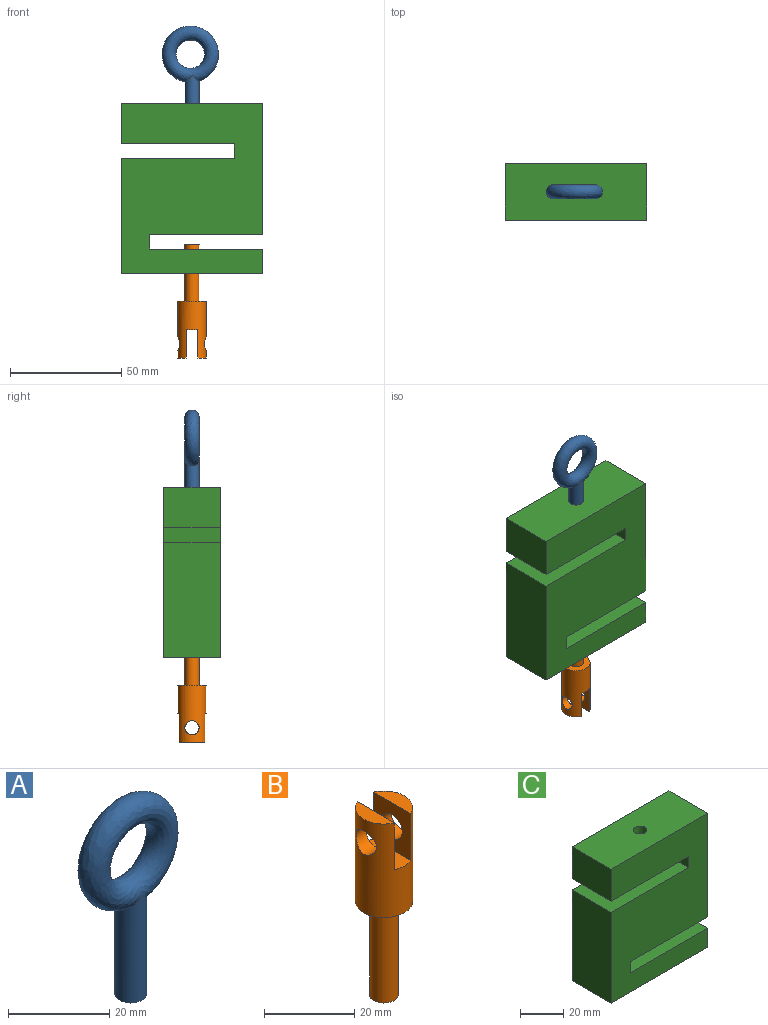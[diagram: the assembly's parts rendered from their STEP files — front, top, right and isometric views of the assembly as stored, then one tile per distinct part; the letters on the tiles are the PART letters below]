
ASSEMBLY  parts=3 mates=2
PART A: 3 faces, bbox 25.1x6.4x47.5 mm
  f0: cylinder r=3.17mm len=25.4mm, axis (0,0,1), area 474.5mm2, adj f1,f2
  f1: plane 6.35x6.35mm, normal (0,0,-1), area 31.7mm2, adj f0
  f2: bspline ~25.26x25.05mm, area 1164.4mm2, adj f0
PART B: 11 faces, bbox 12.7x12.7x50.8 mm
  f0: plane 11.64x3.81mm, normal (0,0,1), area 32mm2, adj f1,f4
  f1: cylinder r=6.35mm len=25.4mm, axis (0,0,-1), area 815.1mm2, adj f0,f2,f3,f4,f5,f6,f7,f8
  f2: plane 11.64x3.81mm, normal (0,0,1), area 32mm2, adj f1,f5
  f3: plane 12.7x12.7mm, normal (0,0,-1), area 95mm2, adj f1,f9
  f4: plane 12.7x11.64mm, normal (-1,0,0), area 116.2mm2, adj f0,f1,f6,f8
  f5: plane 12.7x11.64mm, normal (1,0,0), area 116.2mm2, adj f1,f2,f6,f7
  f6: plane 12.7x5.08mm, normal (0,0,1), area 62.8mm2, adj f1,f4,f5
  f7: cylinder r=3.17mm len=6.35mm, axis (1,0,0), area 67.7mm2, adj f1,f5
  f8: cylinder r=3.17mm len=6.35mm, axis (1,0,0), area 67.7mm2, adj f1,f4
  f9: cylinder r=3.17mm len=25.4mm, axis (0,0,1), area 506.7mm2, adj f3,f10
  f10: plane 6.35x6.35mm, normal (0,0,-1), area 31.7mm2, adj f9
PART C: 16 faces, bbox 63.5x25.4x76.2 mm
  f0: plane 25.4x18.19mm, normal (-1,0,0), area 462mm2, adj f1,f11,f12,f13
  f1: plane 50.8x25.4mm, normal (0,0,-1), area 1258.7mm2, adj f0,f2,f12,f13,f14
  f2: plane 25.4x6.35mm, normal (-1,0,0), area 161.3mm2, adj f1,f3,f12,f13
  f3: plane 50.8x25.4mm, normal (0,0,1), area 1290.3mm2, adj f2,f4,f12,f13
  f4: plane 51.66x25.4mm, normal (-1,0,0), area 1312.2mm2, adj f3,f5,f12,f13
  f5: plane 63.5x25.4mm, normal (0,0,-1), area 1581.2mm2, adj f4,f6,f12,f13,f15
  f6: plane 25.4x10.85mm, normal (1,0,0), area 275.5mm2, adj f5,f7,f12,f13
  f7: plane 50.8x25.4mm, normal (0,0,1), area 1258.7mm2, adj f6,f8,f12,f13,f15
  f8: plane 25.4x6.35mm, normal (1,0,0), area 161.3mm2, adj f7,f9,f12,f13
  f9: plane 50.8x25.4mm, normal (0,0,-1), area 1290.3mm2, adj f8,f10,f12,f13
  f10: plane 59x25.4mm, normal (1,0,0), area 1498.7mm2, adj f9,f11,f12,f13
  f11: plane 63.5x25.4mm, normal (0,0,1), area 1581.2mm2, adj f0,f10,f12,f13,f14
  f12: plane 76.2x63.5mm, normal (0,-1,0), area 4193.5mm2, adj f0,f1,f2,f3,f4,f5,f6,f7
  f13: plane 76.2x63.5mm, normal (0,1,0), area 4193.5mm2, adj f0,f1,f2,f3,f4,f5,f6,f7
  f14: cylinder r=3.17mm len=18.19mm, axis (0,0,1), area 362.9mm2, adj f1,f11
  f15: cylinder r=3.17mm len=10.85mm, axis (0,0,-1), area 216.4mm2, adj f5,f7
PLACE A t=(-44.37,-24.35,52.62)mm
PLACE B rot(axis=(1,0,0),180deg) t=(-44.37,-24.35,-48.9)mm
PLACE C t=(-44.37,-11.65,1.9)mm
MATE cylindrical A.f0 <-> C.f14  axis (0,0,1) through (-44.37,-24.35,40)mm
MATE cylindrical B.f9 <-> C.f14  axis (0,0,-1) through (-44.37,-24.35,-36.2)mm
